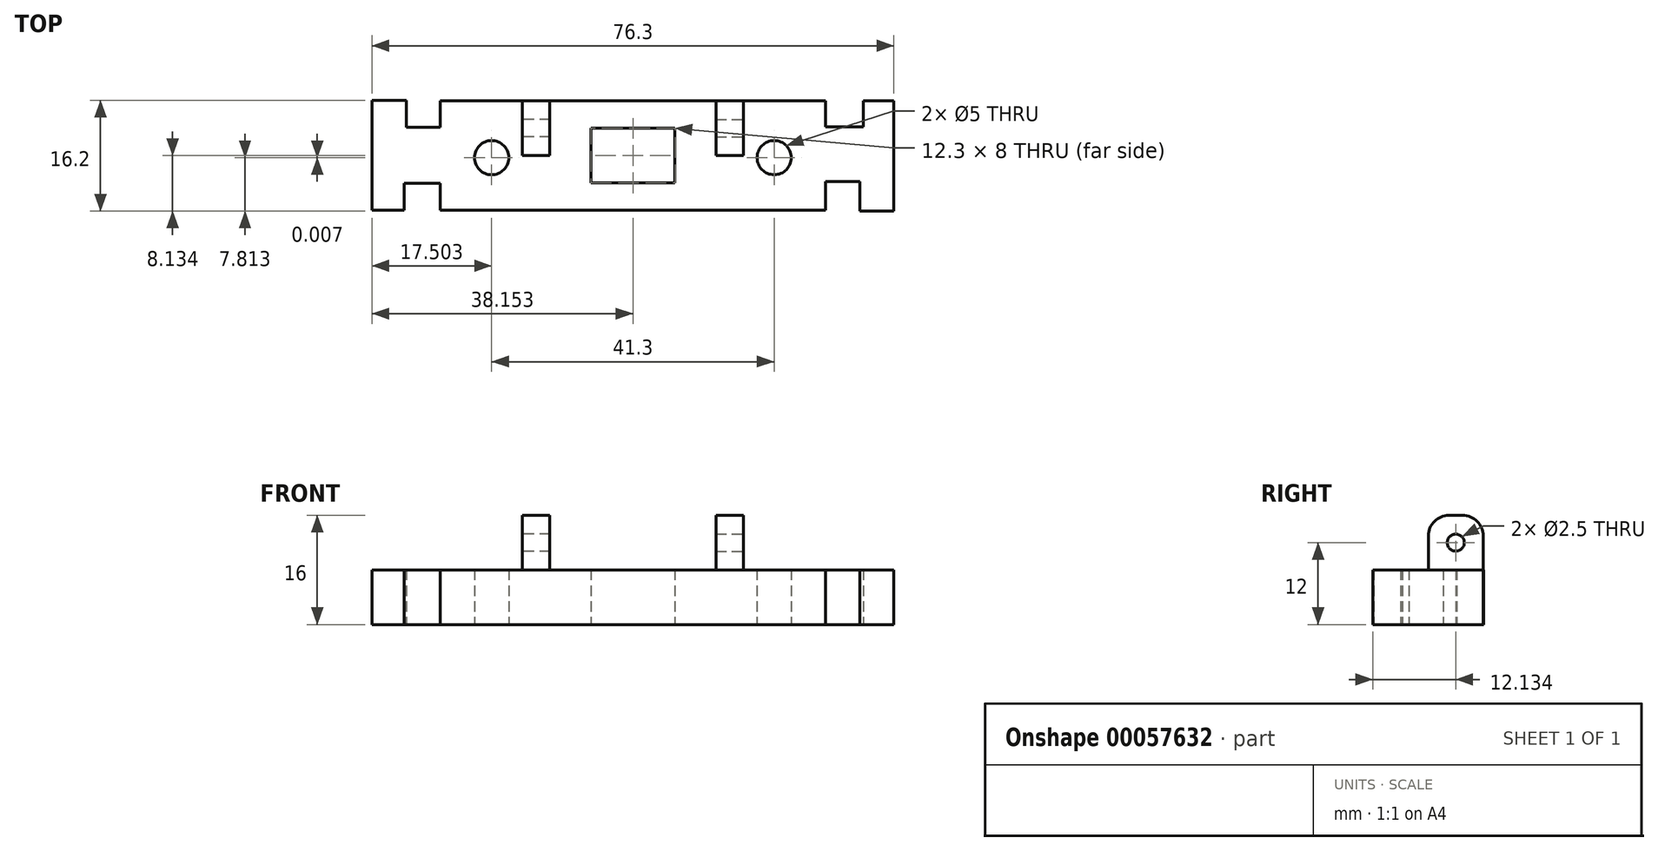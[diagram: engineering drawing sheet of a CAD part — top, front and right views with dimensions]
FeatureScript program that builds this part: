
annotation { "Feature Type Name" : "Feature", "Feature Type Description" : "" }
export const myFeature = defineFeature(function(context is Context, id is Id, definition is map)
    precondition{}
    {
        {
            var Q0;
            Q0=qCreatedBy(makeId("Top.planeOp"),FACE);
            var sketch = newSketch(context, id + "F0", { "sketchPlane" : qUnion([Q0])});
            skLineSegment(sketch, "E0.bottom", {"start": v(-27.38, 8.31) * mm, "end": v(28.92, 8.31) * mm});
            skLineSegment(sketch, "E0.top", {"start": v(-27.38, -7.69) * mm, "end": v(28.92, -7.69) * mm});
            skLineSegment(sketch, "E0.left", {"start": v(-27.38, 8.31) * mm, "end": v(-27.38, -7.69) * mm});
            skLineSegment(sketch, "E0.right", {"start": v(28.92, 8.31) * mm, "end": v(28.92, -7.69) * mm});
            skCircle(sketch, "E1", {"center": v(-19.88, 0) * mm, "radius": 2.5 * mm});
            skCircle(sketch, "E2", {"center": v(21.42, 0) * mm, "radius": 2.5 * mm});
            skLineSegment(sketch, "E3.bottom", {"start": v(-5.38, 4.31) * mm, "end": v(6.92, 4.31) * mm});
            skLineSegment(sketch, "E3.top", {"start": v(-5.38, -3.69) * mm, "end": v(6.92, -3.69) * mm});
            skLineSegment(sketch, "E3.left", {"start": v(-5.38, 4.31) * mm, "end": v(-5.38, -3.69) * mm});
            skLineSegment(sketch, "E3.right", {"start": v(6.92, 4.31) * mm, "end": v(6.92, -3.69) * mm});
            skLineSegment(sketch, "E4", {"start": v(-27.38, 4.45) * mm, "end": v(-32.38, 4.45) * mm});
            skLineSegment(sketch, "E5", {"start": v(-32.38, 4.45) * mm, "end": v(-32.38, 8.38) * mm});
            skLineSegment(sketch, "E6", {"start": v(-32.38, 8.38) * mm, "end": v(-37.38, 8.38) * mm});
            skLineSegment(sketch, "E7", {"start": v(-37.38, 8.38) * mm, "end": v(-37.38, -7.66) * mm});
            skLineSegment(sketch, "E8", {"start": v(-37.38, -7.66) * mm, "end": v(-32.65, -7.66) * mm});
            skLineSegment(sketch, "E9", {"start": v(-32.65, -7.66) * mm, "end": v(-32.65, -3.72) * mm});
            skLineSegment(sketch, "E10", {"start": v(-32.65, -3.72) * mm, "end": v(-27.38, -3.72) * mm});
            skLineSegment(sketch, "E11", {"start": v(28.92, 4.48) * mm, "end": v(34.42, 4.48) * mm});
            skLineSegment(sketch, "E12", {"start": v(34.42, 4.48) * mm, "end": v(34.42, 8.32) * mm});
            skLineSegment(sketch, "E13", {"start": v(34.42, 8.32) * mm, "end": v(38.92, 8.32) * mm});
            skLineSegment(sketch, "E14", {"start": v(38.92, 8.32) * mm, "end": v(38.92, -7.82) * mm});
            skLineSegment(sketch, "E15", {"start": v(38.92, -7.82) * mm, "end": v(33.92, -7.82) * mm});
            skLineSegment(sketch, "E16", {"start": v(33.92, -7.82) * mm, "end": v(33.92, -3.49) * mm});
            skLineSegment(sketch, "E17", {"start": v(33.92, -3.49) * mm, "end": v(28.92, -3.49) * mm});
            skSolve(sketch);
        }
        {
            var Q0;
            Q0 = qSketchRegion(id + "F0", true);
            extrude(context, id + "F1", {"entities" : qUnion([Q0]), "depth" : 8 * mm});
        }
        {
            var Q0;
            Q0=makeQuery(id+"F1.opExtrude","SWEPT_FACE",FACE,{"disambiguationData":[OSD([sQuery(id+"F0.wireOp",EDGE,"E0.bottom")])]});
            var sketch = newSketch(context, id + "F2", { "sketchPlane" : qUnion([Q0])});
            skLineSegment(sketch, "E18.bottom", {"start": v(15.38, 8) * mm, "end": v(11.38, 8) * mm});
            skLineSegment(sketch, "E18.top", {"start": v(15.38, 16) * mm, "end": v(11.38, 16) * mm});
            skLineSegment(sketch, "E18.left", {"start": v(15.38, 8) * mm, "end": v(15.38, 16) * mm});
            skLineSegment(sketch, "E18.right", {"start": v(11.38, 8) * mm, "end": v(11.38, 16) * mm});
            skLineSegment(sketch, "E19.bottom", {"start": v(-12.92, 8) * mm, "end": v(-16.92, 8) * mm});
            skLineSegment(sketch, "E19.top", {"start": v(-12.92, 16) * mm, "end": v(-16.92, 16) * mm});
            skLineSegment(sketch, "E19.left", {"start": v(-12.92, 8) * mm, "end": v(-12.92, 16) * mm});
            skLineSegment(sketch, "E19.right", {"start": v(-16.92, 8) * mm, "end": v(-16.92, 16) * mm});
            skSolve(sketch);
        }
        {
            var Q0;
            Q0 = qSketchRegion(id + "F2", true);
            extrude(context, id + "F3", {"entities" : qUnion([Q0]), "oppositeDirection" : true, "depth" : 8 * mm});
        }
        {
            var Q0;
            Q0=makeQuery(id+"F3.opExtrude","CAP_EDGE",EDGE,{"disambiguationData":[OSD([sQuery(id+"F2.wireOp",EDGE,"E19.top")])],"isStart":true});
            var Q1;
            Q1=makeQuery(id+"F3.opExtrude","CAP_EDGE",EDGE,{"disambiguationData":[OSD([sQuery(id+"F2.wireOp",EDGE,"E19.top")])],"isStart":false});
            var Q2;
            Q2=makeQuery(id+"F3.opExtrude","CAP_EDGE",EDGE,{"disambiguationData":[OSD([sQuery(id+"F2.wireOp",EDGE,"E18.top")])],"isStart":true});
            var Q3;
            Q3=makeQuery(id+"F3.opExtrude","CAP_EDGE",EDGE,{"disambiguationData":[OSD([sQuery(id+"F2.wireOp",EDGE,"E18.top")])],"isStart":false});
            fillet(context, id + "F4", {"entities" : qUnion([Q0, Q1, Q2, Q3]), "radius" : 3 * mm, "tangentPropagation" : true, "allowEdgeOverflow" : false});
        }
        {
            var Q0;
            Q0=makeQuery(id+"F3.opExtrude","SWEPT_FACE",FACE,{"disambiguationData":[OSD([sQuery(id+"F2.wireOp",EDGE,"E18.left")])]});
            var sketch = newSketch(context, id + "F5", { "sketchPlane" : qUnion([Q0])});
            skCircle(sketch, "E20", {"center": v(-4.31, 12) * mm, "radius": 1.25 * mm});
            skSolve(sketch);
        }
        {
            var Q0;
            Q0=sQuery(id+"F5.wireOp",VERTEX,"E20.center");
            var Q1;
            Q1=makeQuery(id+"F3.opExtrude","SWEPT_BODY",BODY,{"disambiguationData":[OSD([sQuery(id+"F2.wireOp",EDGE,"E18.bottom"),sQuery(id+"F2.wireOp",EDGE,"E18.top"),sQuery(id+"F2.wireOp",EDGE,"E18.left"),sQuery(id+"F2.wireOp",EDGE,"E18.right")])]});
            hole(context, id + "F6", {"style" : HoleStyle.SIMPLE, "holeDiameter" : 2.5 * mm, "endStyle" : HoleEndStyle.THROUGH, "locations" : qUnion([Q0]), "scope" : qUnion([Q1])});
        }
        {
            var Q0;
            Q0=makeQuery(id+"F3.opExtrude","SWEPT_FACE",FACE,{"disambiguationData":[OSD([sQuery(id+"F2.wireOp",EDGE,"E19.right")])]});
            var sketch = newSketch(context, id + "F7", { "sketchPlane" : qUnion([Q0])});
            skCircle(sketch, "E21", {"center": v(4.31, 12) * mm, "radius": 1.25 * mm});
            skSolve(sketch);
        }
        {
            var Q0;
            Q0=sQuery(id+"F7.wireOp",VERTEX,"E21.center");
            var Q1;
            Q1=makeQuery(id+"F3.opExtrude","SWEPT_BODY",BODY,{"disambiguationData":[OSD([sQuery(id+"F2.wireOp",EDGE,"E19.bottom"),sQuery(id+"F2.wireOp",EDGE,"E19.top"),sQuery(id+"F2.wireOp",EDGE,"E19.left"),sQuery(id+"F2.wireOp",EDGE,"E19.right")])]});
            hole(context, id + "F8", {"style" : HoleStyle.SIMPLE, "holeDiameter" : 2.5 * mm, "endStyle" : HoleEndStyle.THROUGH, "locations" : qUnion([Q0]), "scope" : qUnion([Q1])});
        }
    });
